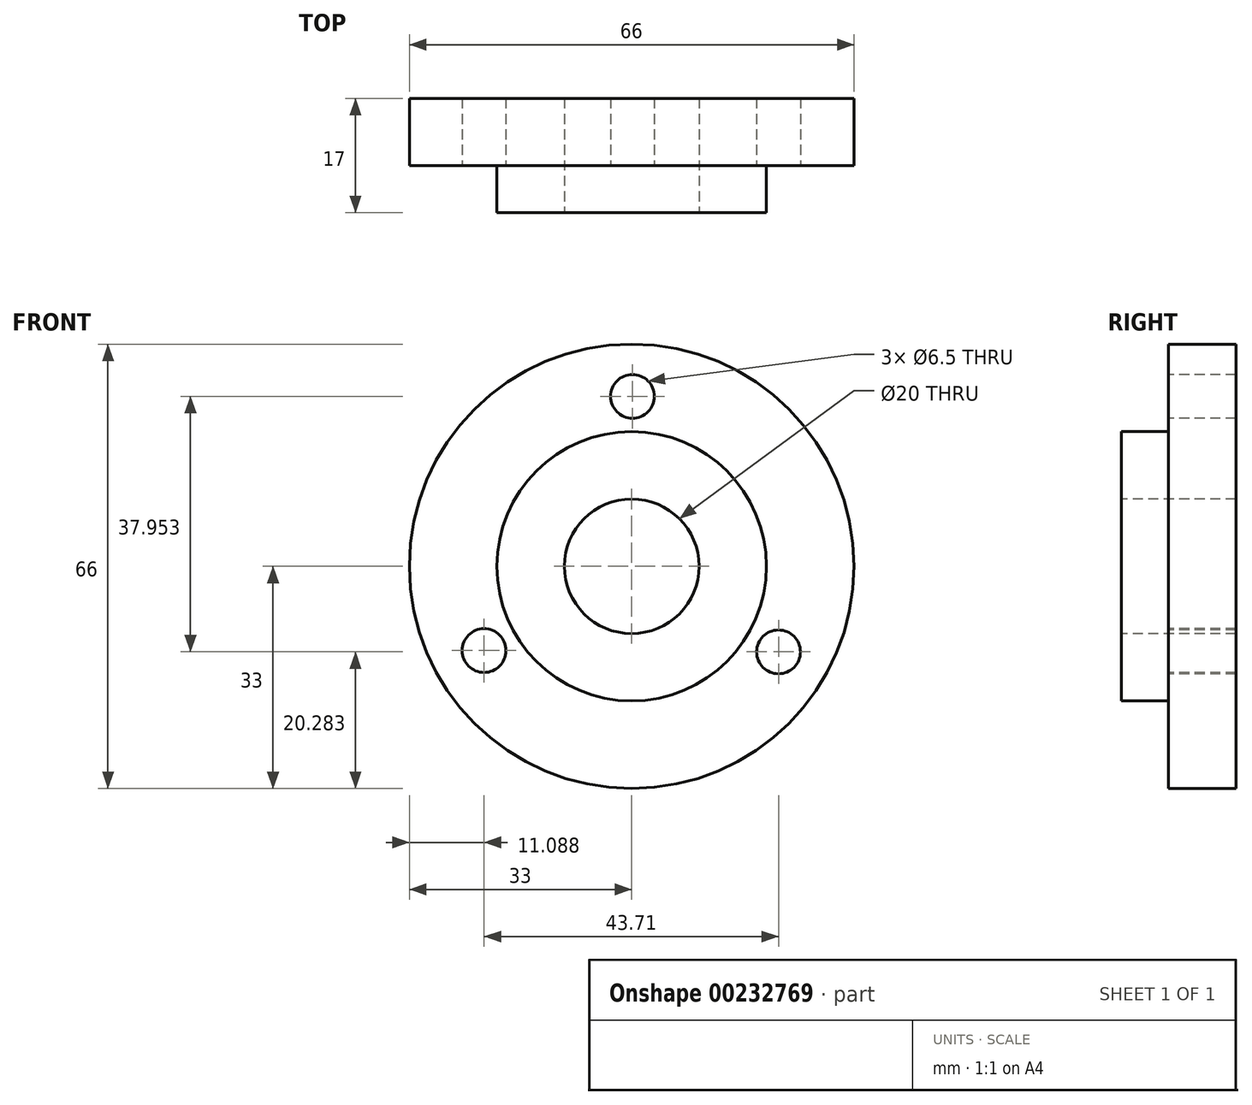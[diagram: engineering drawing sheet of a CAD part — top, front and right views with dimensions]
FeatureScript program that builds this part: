
annotation { "Feature Type Name" : "Feature", "Feature Type Description" : "" }
export const myFeature = defineFeature(function(context is Context, id is Id, definition is map)
    precondition{}
    {
        {
            var Q0;
            Q0=qCreatedBy(makeId("Front.planeOp"),FACE);
            var sketch = newSketch(context, id + "F0", { "sketchPlane" : qUnion([Q0])});
            skCircle(sketch, "E0", {"center": v(0, 0) * mm, "radius": 33 * mm});
            skCircle(sketch, "E1", {"center": v(0, 0) * mm, "radius": 20 * mm});
            skCircle(sketch, "E2", {"center": v(0, 0) * mm, "radius": 10 * mm});
            skPoint(sketch, "E3.center", {"position": v(0, 0.24) * mm});
            skLineSegment(sketch, "E4", {"start": v(3.36, 25.24) * mm, "end": v(9.4, 25.24) * mm});
            skCircle(sketch, "E5", {"center": v(0.11, 25.24) * mm, "radius": 3.25 * mm});
            skPoint(sketch, "E6.orphan", {"position": v(-9.16, 25.24) * mm});
            skCircle(sketch, "E7.1.0", {"center": v(-21.91, -12.52) * mm, "radius": 3.25 * mm});
            skCircle(sketch, "E7.2.0", {"center": v(21.8, -12.72) * mm, "radius": 3.25 * mm});
            skSolve(sketch);
        }
        {
            var Q0;
            Q0=makeQuery(id+"F0.imprint","IMPRINT",FACE,{"disambiguationData":[TD([[makeQuery(id+"F0.imprint","IMPRINT",EDGE,{"derivedFrom":sQuery(id+"F0.wireOp",EDGE,"E1")}),1.0]])]});
            var Q1;
            Q1=makeQuery(id+"F0.imprint","IMPRINT",FACE,{"disambiguationData":[TD([[makeQuery(id+"F0.imprint","IMPRINT",EDGE,{"derivedFrom":sQuery(id+"F0.wireOp",EDGE,"E0")}),1.0]])]});
            extrude(context, id + "F1", {"entities" : qUnion([Q0, Q1]), "oppositeDirection" : true, "depth" : 10 * mm});
        }
        {
            var Q0;
            Q0=makeQuery(id+"F0.imprint","IMPRINT",FACE,{"disambiguationData":[TD([[makeQuery(id+"F0.imprint","IMPRINT",EDGE,{"derivedFrom":sQuery(id+"F0.wireOp",EDGE,"E1")}),1.0]])]});
            extrude(context, id + "F2", {"entities" : qUnion([Q0]), "operationType" : NewBodyOperationType.ADD, "depth" : 7 * mm});
        }
    });
